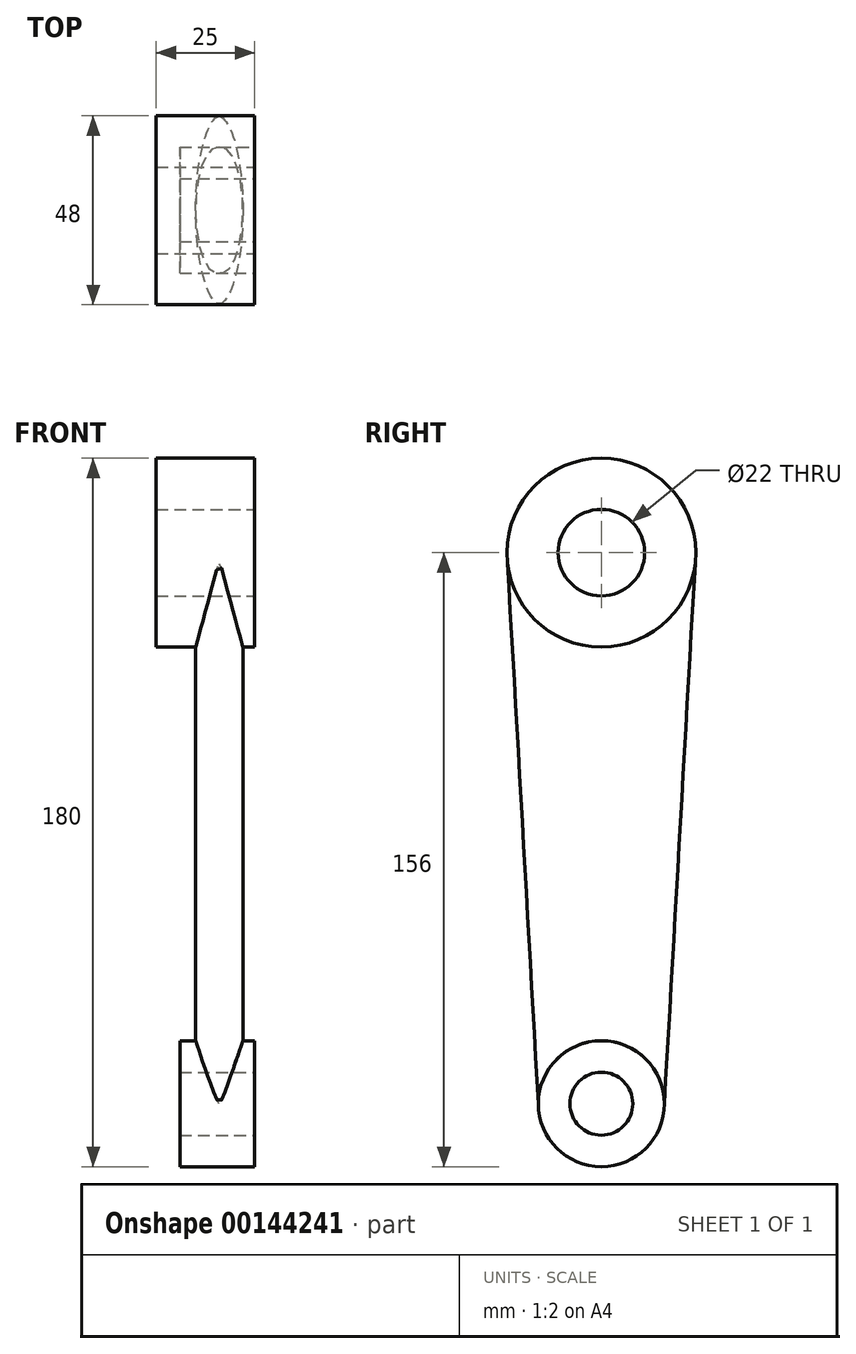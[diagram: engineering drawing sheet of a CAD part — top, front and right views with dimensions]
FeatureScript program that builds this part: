
annotation { "Feature Type Name" : "Feature", "Feature Type Description" : "" }
export const myFeature = defineFeature(function(context is Context, id is Id, definition is map)
    precondition{}
    {
        {
            var Q0;
            Q0=qCreatedBy(makeId("Right.planeOp"),FACE);
            var sketch = newSketch(context, id + "F0", { "sketchPlane" : qUnion([Q0])});
            skCircle(sketch, "E0", {"center": v(0, 0) * mm, "radius": 8 * mm});
            skCircle(sketch, "E1", {"center": v(0, 0) * mm, "radius": 16 * mm});
            skCircle(sketch, "E2", {"center": v(0, 140) * mm, "radius": 11 * mm});
            skCircle(sketch, "E3", {"center": v(0, 140) * mm, "radius": 24 * mm});
            skSolve(sketch);
        }
        {
            var Q0;
            Q0=makeQuery(id+"F0.imprint","IMPRINT",FACE,{"disambiguationData":[TD([[makeQuery(id+"F0.imprint","IMPRINT",EDGE,{"derivedFrom":sQuery(id+"F0.wireOp",EDGE,"E0")}),-1.0]])]});
            extrude(context, id + "F1", {"entities" : qUnion([Q0]), "oppositeDirection" : true, "depth" : 19 * mm});
        }
        {
            var Q0;
            Q0=makeQuery(id+"F0.imprint","IMPRINT",FACE,{"disambiguationData":[TD([[makeQuery(id+"F0.imprint","IMPRINT",EDGE,{"derivedFrom":sQuery(id+"F0.wireOp",EDGE,"E2")}),-1.0]])]});
            extrude(context, id + "F2", {"entities" : qUnion([Q0]), "oppositeDirection" : true, "depth" : 25 * mm});
        }
        {
            var Q0;
            Q0=qCreatedBy(makeId("Top.planeOp"),FACE);
            var sketch = newSketch(context, id + "F3", { "sketchPlane" : qUnion([Q0])});
            skEllipse(sketch, "E4", {"center": v(-9, 0) * mm, "majorRadius": 16 * mm, "minorRadius": 6 * mm, "majorAxis": v(0, 1)});
            skPoint(sketch, "E5", {"position": v(-3, 0) * mm});
            skLineSegment(sketch, "E6", {"start": v(0, -16) * mm, "end": v(-19, -16) * mm, "construction": true});
            skSolve(sketch);
        }
        {
            var Q0;
            Q0=sQuery(id+"F0.wireOp",VERTEX,"E2.center");
            var Q1;
            Q1=qCreatedBy(makeId("Top.planeOp"),FACE);
            cPlane(context, id + "F4", {"entities" : qUnion([Q0, Q1]), "cplaneType" : CPlaneType.PLANE_POINT, "offset" : 25 * mm, "width" : 150 * mm, "height" : 150 * mm});
        }
        {
            var Q0;
            Q0=qCreatedBy(id+"F4.planeOp",FACE);
            var sketch = newSketch(context, id + "F5", { "sketchPlane" : qUnion([Q0])});
            skEllipse(sketch, "E7", {"center": v(-9, 0) * mm, "majorRadius": 24 * mm, "minorRadius": 6 * mm, "majorAxis": v(0, 1)});
            skPoint(sketch, "E8", {"position": v(-3, 0) * mm});
            skLineSegment(sketch, "E9", {"start": v(0, -24) * mm, "end": v(-25, -24) * mm, "construction": true});
            skSolve(sketch);
        }
        {
            var Q0;
            Q0=makeQuery(id+"F5.imprint","IMPRINT",FACE,{"disambiguationData":[TD([[makeQuery(id+"F5.imprint","IMPRINT",EDGE,{"derivedFrom":sQuery(id+"F5.wireOp",EDGE,"E7")}),1.0]])]});
            var Q1;
            Q1=makeQuery(id+"F3.imprint","IMPRINT",FACE,{"disambiguationData":[TD([[makeQuery(id+"F3.imprint","IMPRINT",EDGE,{"derivedFrom":sQuery(id+"F3.wireOp",EDGE,"E4")}),1.0]])]});
            loft(context, id + "F6", {"operationType" : NewBodyOperationType.ADD, "sheetProfilesArray" : [{ "sheetProfileEntities" : qUnion([Q0]) }, { "sheetProfileEntities" : qUnion([Q1]) }]});
        }
        {
            var Q0;
            Q0=makeQuery(id+"F0.imprint","IMPRINT",FACE,{"disambiguationData":[TD([[makeQuery(id+"F0.imprint","IMPRINT",EDGE,{"derivedFrom":sQuery(id+"F0.wireOp",EDGE,"E2")}),1.0]])]});
            var Q1;
            Q1=makeQuery(id+"F0.imprint","IMPRINT",FACE,{"disambiguationData":[TD([[makeQuery(id+"F0.imprint","IMPRINT",EDGE,{"derivedFrom":sQuery(id+"F0.wireOp",EDGE,"E0")}),1.0]])]});
            extrude(context, id + "F7", {"entities" : qUnion([Q0, Q1]), "operationType" : NewBodyOperationType.REMOVE, "endBound" : BoundingType.THROUGH_ALL, "oppositeDirection" : true, "depth" : 25 * mm});
        }
    });
